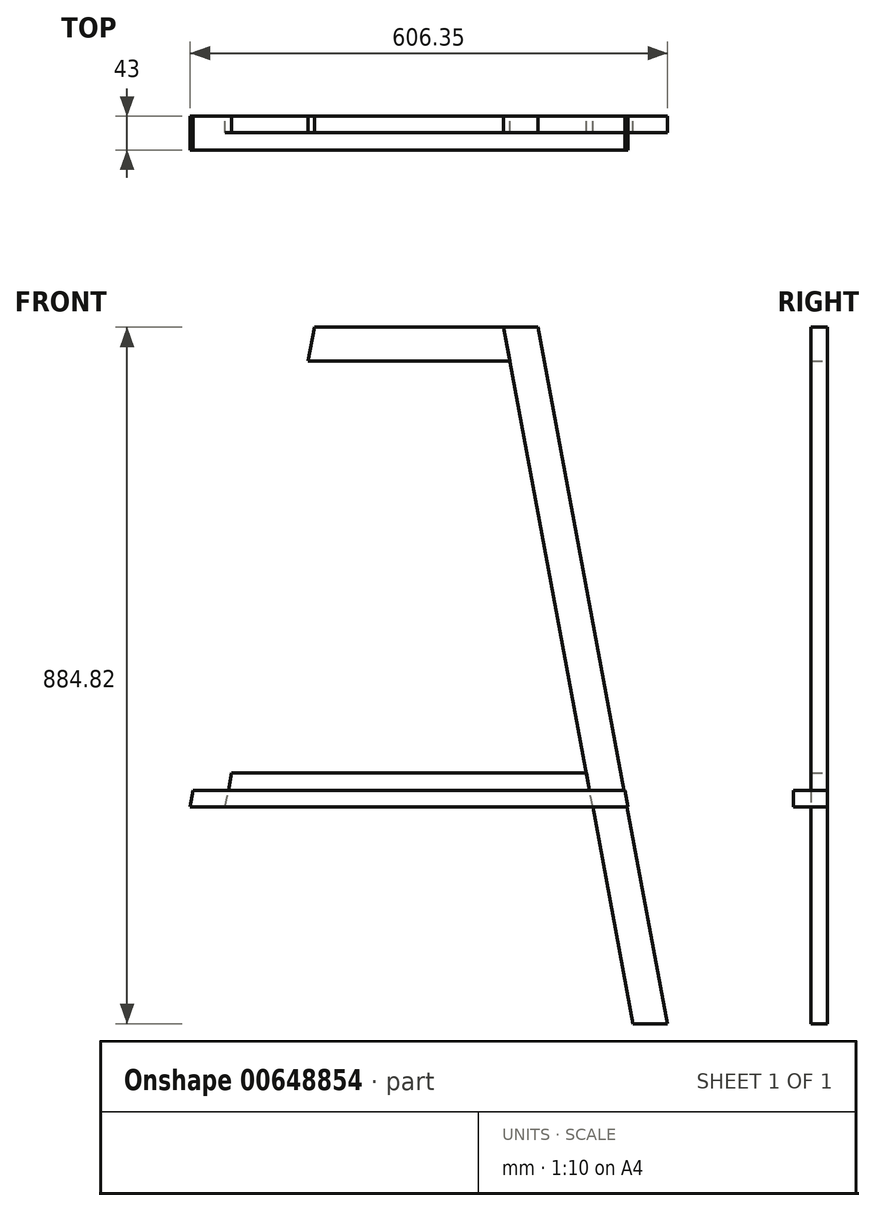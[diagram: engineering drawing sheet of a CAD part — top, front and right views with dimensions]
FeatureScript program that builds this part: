
annotation { "Feature Type Name" : "Feature", "Feature Type Description" : "" }
export const myFeature = defineFeature(function(context is Context, id is Id, definition is map)
    precondition{}
    {
        {
            assignVariable(context, id + "F0", {"name" : "BeamW", "anyValue" : 43});
        }
        {
            assignVariable(context, id + "F1", {"name" : "BeamH", "anyValue" : 21});
        }
        {
            var Q0;
            Q0=qCreatedBy(makeId("Front.planeOp"),FACE);
            var sketch = newSketch(context, id + "F2", { "sketchPlane" : qUnion([Q0])});
            skLineSegment(sketch, "E0.bottom", {"start": v(0, 0) * mm, "end": v(720, 0) * mm, "construction": true});
            skLineSegment(sketch, "E0.top", {"start": v(0, 180) * mm, "end": v(720, 180) * mm, "construction": true});
            skLineSegment(sketch, "E0.left", {"start": v(0, 0) * mm, "end": v(0, 180) * mm, "construction": true});
            skLineSegment(sketch, "E0.right", {"start": v(720, 0) * mm, "end": v(720, 180) * mm, "construction": true});
            skLineSegment(sketch, "E1.top", {"start": v(0, 900) * mm, "end": v(720, 900) * mm, "construction": true});
            skLineSegment(sketch, "E1.left", {"start": v(0, 180) * mm, "end": v(0, 900) * mm, "construction": true});
            skLineSegment(sketch, "E1.right", {"start": v(720, 180) * mm, "end": v(720, 900) * mm, "construction": true});
            skLineSegment(sketch, "E2", {"start": v(360, 900) * mm, "end": v(360, 0) * mm, "construction": true});
            skSolve(sketch);
        }
        {
            var Q0;
            Q0=qCreatedBy(makeId("Front.planeOp"),FACE);
            var sketch = newSketch(context, id + "F3", { "sketchPlane" : qUnion([Q0])});
            skLineSegment(sketch, "E3.0", {"start": v(0, 900) * mm, "end": v(720, 900) * mm, "construction": true});
            skLineSegment(sketch, "E4", {"start": v(523.74, 900) * mm, "end": v(688.35, 15.18) * mm});
            skLineSegment(sketch, "E5", {"start": v(688.35, 15.18) * mm, "end": v(644.62, 15.18) * mm});
            skLineSegment(sketch, "E6", {"start": v(644.62, 15.18) * mm, "end": v(480, 900) * mm});
            skLineSegment(sketch, "E7", {"start": v(480, 900) * mm, "end": v(523.74, 900) * mm});
            skLineSegment(sketch, "E8", {"start": v(523.74, 900) * mm, "end": v(481.46, 892.13) * mm, "construction": true});
            skSolve(sketch);
        }
        {
            var Q0;
            Q0=qCreatedBy(makeId("Front.planeOp"),FACE);
            var sketch = newSketch(context, id + "F4", { "sketchPlane" : qUnion([Q0])});
            skLineSegment(sketch, "E9.0", {"start": v(644.62, 15.18) * mm, "end": v(480, 900) * mm, "construction": true});
            skLineSegment(sketch, "E10.0", {"start": v(480, 900) * mm, "end": v(523.74, 900) * mm, "construction": true});
            skLineSegment(sketch, "E11.0", {"start": v(523.74, 900) * mm, "end": v(688.35, 15.18) * mm, "construction": true});
            skLineSegment(sketch, "E12", {"start": v(593.4, 290.46) * mm, "end": v(480, 900) * mm});
            skLineSegment(sketch, "E13", {"start": v(480, 900) * mm, "end": v(523.74, 900) * mm});
            skLineSegment(sketch, "E14", {"start": v(523.74, 900) * mm, "end": v(637.14, 290.46) * mm});
            skLineSegment(sketch, "E15", {"start": v(637.14, 290.46) * mm, "end": v(593.4, 290.46) * mm});
            skSolve(sketch);
        }
        {
            var Q0;
            Q0=qCreatedBy(makeId("Front.planeOp"),FACE);
            var sketch = newSketch(context, id + "F5", { "sketchPlane" : qUnion([Q0])});
            skLineSegment(sketch, "E16.0", {"start": v(644.62, 15.18) * mm, "end": v(480, 900) * mm, "construction": true});
            skLineSegment(sketch, "E17.0", {"start": v(360, 900) * mm, "end": v(360, 0) * mm, "construction": true});
            skLineSegment(sketch, "E18", {"start": v(360, 900) * mm, "end": v(480, 900) * mm});
            skLineSegment(sketch, "E19", {"start": v(480, 900) * mm, "end": v(488, 857) * mm});
            skLineSegment(sketch, "E20", {"start": v(488, 857) * mm, "end": v(360, 857) * mm});
            skLineSegment(sketch, "E21.MirrorCS", {"start": v(360, 900) * mm, "end": v(240, 900) * mm});
            skLineSegment(sketch, "E22.MirrorCS", {"start": v(240, 900) * mm, "end": v(232, 857) * mm});
            skLineSegment(sketch, "E23.MirrorCS", {"start": v(232, 857) * mm, "end": v(360, 857) * mm});
            skSolve(sketch);
        }
        {
            var Q0;
            Q0=qCreatedBy(makeId("Front.planeOp"),FACE);
            var sketch = newSketch(context, id + "F6", { "sketchPlane" : qUnion([Q0])});
            skLineSegment(sketch, "E24.0", {"start": v(593.4, 290.46) * mm, "end": v(480, 900) * mm, "construction": true});
            skLineSegment(sketch, "E25.0", {"start": v(360, 900) * mm, "end": v(360, 0) * mm, "construction": true});
            skLineSegment(sketch, "E26", {"start": v(360, 290.46) * mm, "end": v(593.4, 290.46) * mm});
            skLineSegment(sketch, "E27", {"start": v(593.4, 290.46) * mm, "end": v(585.4, 333.46) * mm});
            skLineSegment(sketch, "E28", {"start": v(585.4, 333.46) * mm, "end": v(360, 333.46) * mm});
            skLineSegment(sketch, "E29.MirrorCS", {"start": v(134.6, 333.46) * mm, "end": v(360, 333.46) * mm});
            skLineSegment(sketch, "E30.MirrorCS", {"start": v(126.6, 290.46) * mm, "end": v(134.6, 333.46) * mm});
            skLineSegment(sketch, "E31.MirrorCS", {"start": v(360, 290.46) * mm, "end": v(126.6, 290.46) * mm});
            skSolve(sketch);
        }
        {
            var Q0;
            Q0=qCreatedBy(makeId("Front.planeOp"),FACE);
            var sketch = newSketch(context, id + "F7", { "sketchPlane" : qUnion([Q0])});
            skLineSegment(sketch, "E32.0", {"start": v(637.14, 290.46) * mm, "end": v(593.4, 290.46) * mm, "construction": true});
            skLineSegment(sketch, "E33.0", {"start": v(523.74, 900) * mm, "end": v(637.14, 290.46) * mm, "construction": true});
            skLineSegment(sketch, "E34.0", {"start": v(360, 900) * mm, "end": v(360, 0) * mm, "construction": true});
            skLineSegment(sketch, "E35", {"start": v(360, 290.46) * mm, "end": v(638, 290.46) * mm});
            skPoint(sketch, "E35.startSnap0", {"position": v(615.27, 290.46) * mm});
            skLineSegment(sketch, "E36", {"start": v(638, 290.46) * mm, "end": v(634.1, 311.46) * mm});
            skLineSegment(sketch, "E37", {"start": v(634.1, 311.46) * mm, "end": v(360, 311.46) * mm});
            skLineSegment(sketch, "E38.MirrorCS", {"start": v(85.9, 311.46) * mm, "end": v(360, 311.46) * mm});
            skLineSegment(sketch, "E39.MirrorCS", {"start": v(82, 290.46) * mm, "end": v(85.9, 311.46) * mm});
            skLineSegment(sketch, "E40.MirrorCS", {"start": v(360, 290.46) * mm, "end": v(82, 290.46) * mm});
            skSolve(sketch);
        }
        {
            var Q0;
            Q0=makeQuery(id+"F3.imprint","IMPRINT",FACE,{"disambiguationData":[TD([[makeQuery(id+"F3.imprint","IMPRINT",EDGE,{"derivedFrom":sQuery(id+"F3.wireOp",EDGE,"E4")}),-1.0]])]});
            extrude(context, id + "F8", {"entities" : qUnion([Q0]), "depth" : (getVariable(context, 'BeamH')) * mm, "offsetDistance" : 25 * mm});
        }
        {
            var Q0;
            Q0=makeQuery(id+"F4.imprint","IMPRINT",FACE,{"disambiguationData":[TD([[makeQuery(id+"F4.imprint","IMPRINT",EDGE,{"derivedFrom":sQuery(id+"F4.wireOp",EDGE,"E12")}),-1.0]])]});
            extrude(context, id + "F9", {"entities" : qUnion([Q0]), "depth" : (getVariable(context, 'BeamH')) * mm, "offsetDistance" : 25 * mm});
        }
        {
            var Q0;
            Q0=makeQuery(id+"F5.imprint","IMPRINT",FACE,{"disambiguationData":[TD([[makeQuery(id+"F5.imprint","IMPRINT",EDGE,{"derivedFrom":sQuery(id+"F5.wireOp",EDGE,"E18")}),-1.0]])]});
            extrude(context, id + "F10", {"entities" : qUnion([Q0]), "depth" : (getVariable(context, 'BeamH')) * mm, "offsetDistance" : 25 * mm});
        }
        {
            var Q0;
            Q0=makeQuery(id+"F6.imprint","IMPRINT",FACE,{"disambiguationData":[TD([[makeQuery(id+"F6.imprint","IMPRINT",EDGE,{"derivedFrom":sQuery(id+"F6.wireOp",EDGE,"E26")}),1.0]])]});
            extrude(context, id + "F11", {"entities" : qUnion([Q0]), "depth" : (getVariable(context, 'BeamH')) * mm, "offsetDistance" : 25 * mm});
        }
        {
            var Q0;
            Q0=makeQuery(id+"F7.imprint","IMPRINT",FACE,{"disambiguationData":[TD([[makeQuery(id+"F7.imprint","IMPRINT",EDGE,{"derivedFrom":sQuery(id+"F7.wireOp",EDGE,"E35")}),1.0]])]});
            extrude(context, id + "F12", {"entities" : qUnion([Q0]), "depth" : (getVariable(context, 'BeamW')) * mm, "offsetDistance" : 25 * mm});
        }
    });
